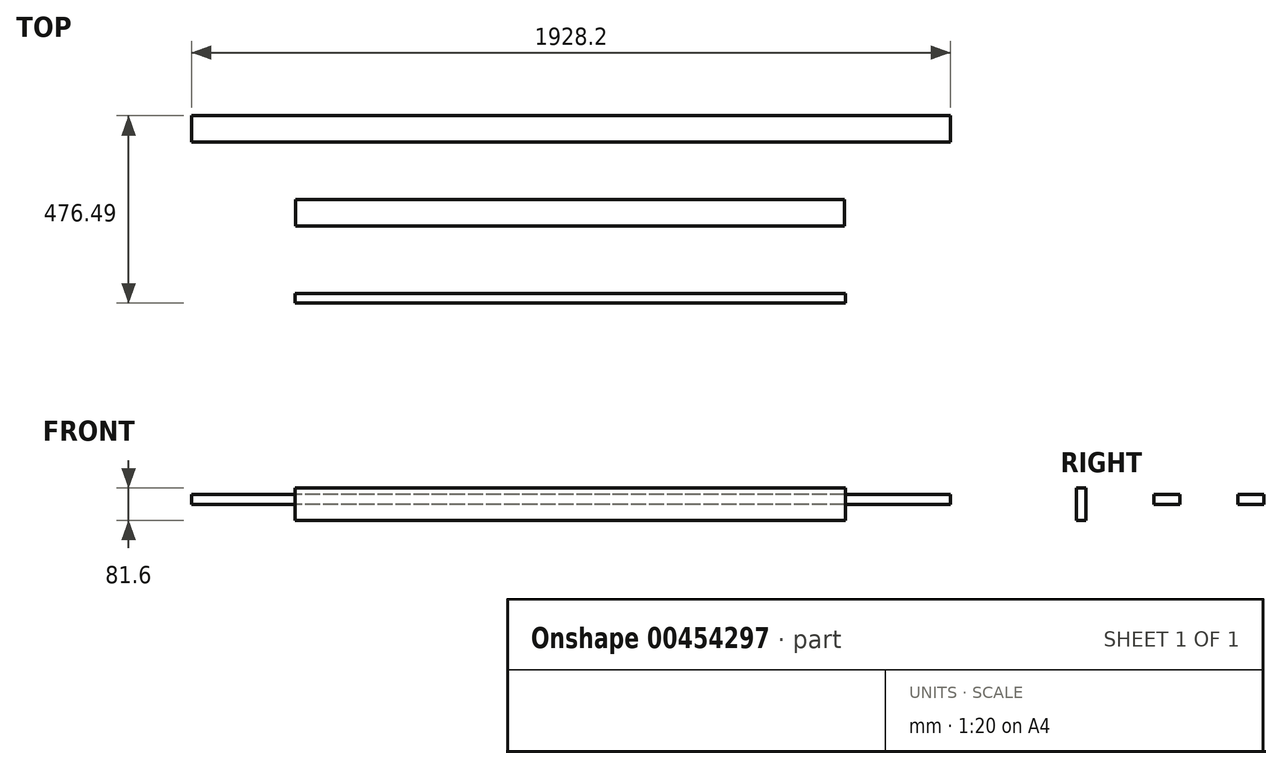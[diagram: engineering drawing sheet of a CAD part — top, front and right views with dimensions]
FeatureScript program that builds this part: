
annotation { "Feature Type Name" : "Feature", "Feature Type Description" : "" }
export const myFeature = defineFeature(function(context is Context, id is Id, definition is map)
    precondition{}
    {
        {
            var Q0;
            Q0=qCreatedBy(makeId("Front.planeOp"),FACE);
            var sketch = newSketch(context, id + "F0", { "sketchPlane" : qUnion([Q0])});
            skLineSegment(sketch, "E0.bottom", {"start": v(698.9, -40.8) * mm, "end": v(-698.9, -40.8) * mm});
            skLineSegment(sketch, "E0.top", {"start": v(698.9, 40.8) * mm, "end": v(-698.9, 40.8) * mm});
            skLineSegment(sketch, "E0.left", {"start": v(698.9, -40.8) * mm, "end": v(698.9, 40.8) * mm});
            skLineSegment(sketch, "E0.right", {"start": v(-698.9, -40.8) * mm, "end": v(-698.9, 40.8) * mm});
            skPoint(sketch, "E0.middle", {"position": v(0, 0) * mm});
            skSolve(sketch);
        }
        {
            var Q0;
            Q0=makeQuery(id+"F0.imprint","IMPRINT",FACE,{"disambiguationData":[TD([[makeQuery(id+"F0.imprint","IMPRINT",EDGE,{"derivedFrom":sQuery(id+"F0.wireOp",EDGE,"E0.bottom")}),-1.0]])]});
            extrude(context, id + "F1", {"entities" : qUnion([Q0]), "depth" : 24.5 * mm});
        }
        {
            var Q0;
            Q0=qCreatedBy(makeId("Top.planeOp"),FACE);
            var sketch = newSketch(context, id + "F2", { "sketchPlane" : qUnion([Q0])});
            skLineSegment(sketch, "E1.bottom", {"start": v(697, 171.9) * mm, "end": v(-697, 171.9) * mm});
            skLineSegment(sketch, "E1.top", {"start": v(697, 238.5) * mm, "end": v(-697, 238.5) * mm});
            skLineSegment(sketch, "E1.left", {"start": v(697, 171.9) * mm, "end": v(697, 238.5) * mm});
            skLineSegment(sketch, "E1.right", {"start": v(-697, 171.9) * mm, "end": v(-697, 238.5) * mm});
            skPoint(sketch, "E1.middle", {"position": v(0, 205.2) * mm});
            skSolve(sketch);
        }
        {
            var Q0;
            Q0 = qSketchRegion(id + "F2", true);
            extrude(context, id + "F3", {"entities" : qUnion([Q0]), "depth" : 25 * mm});
        }
        {
            var Q0;
            Q0=qCreatedBy(makeId("Top.planeOp"),FACE);
            var sketch = newSketch(context, id + "F4", { "sketchPlane" : qUnion([Q0])});
            skLineSegment(sketch, "E2.bottom", {"start": v(966.14, 385.4) * mm, "end": v(-962.06, 385.4) * mm});
            skLineSegment(sketch, "E2.top", {"start": v(966.14, 452) * mm, "end": v(-962.06, 452) * mm});
            skLineSegment(sketch, "E2.left", {"start": v(966.14, 385.4) * mm, "end": v(966.14, 452) * mm});
            skLineSegment(sketch, "E2.right", {"start": v(-962.06, 385.4) * mm, "end": v(-962.06, 452) * mm});
            skPoint(sketch, "E2.middle", {"position": v(2.04, 418.7) * mm});
            skSolve(sketch);
        }
        {
            var Q0;
            Q0 = qSketchRegion(id + "F4", true);
            extrude(context, id + "F5", {"entities" : qUnion([Q0]), "depth" : 25 * mm});
        }
    });
